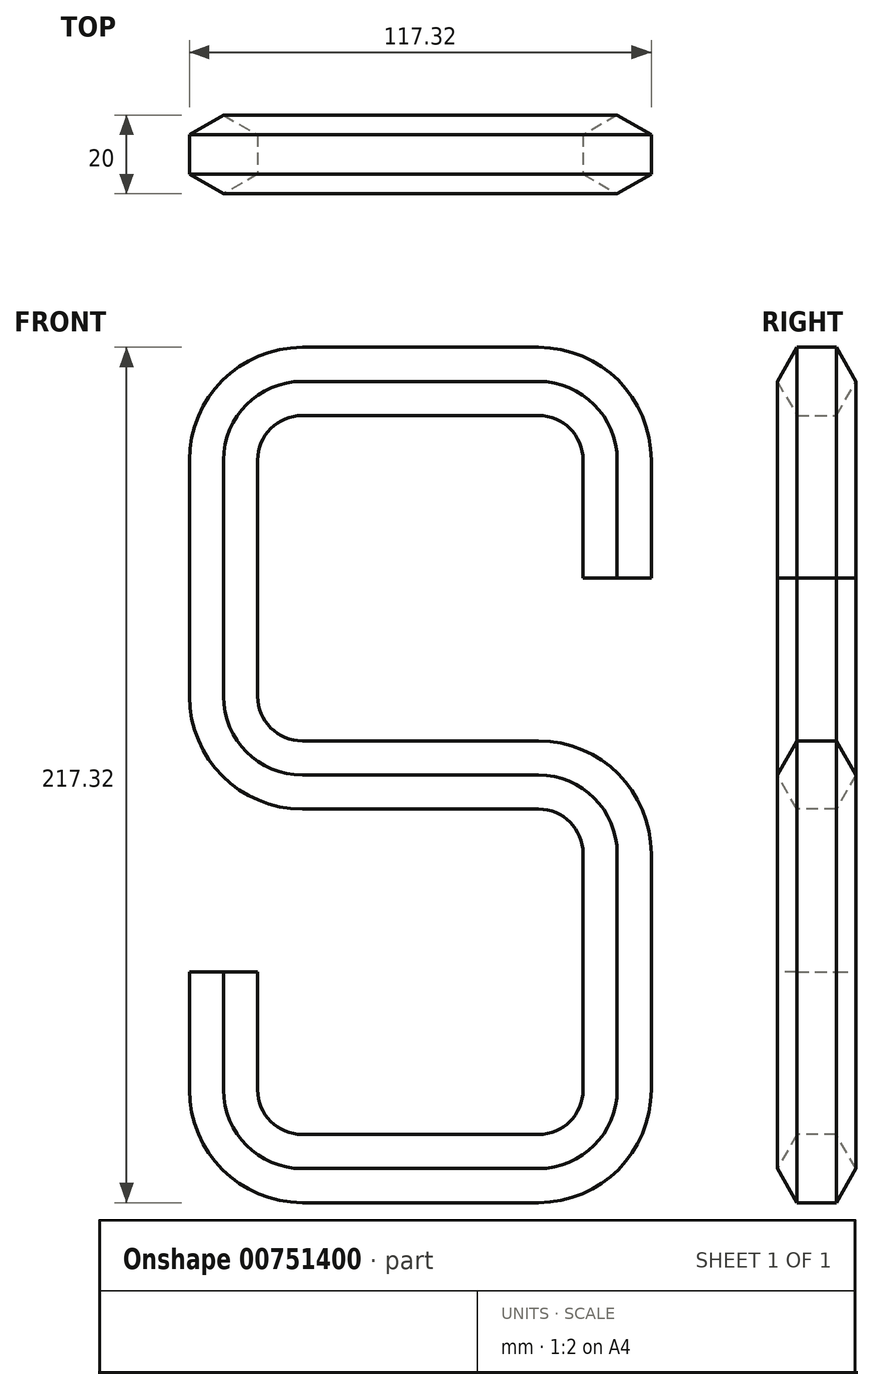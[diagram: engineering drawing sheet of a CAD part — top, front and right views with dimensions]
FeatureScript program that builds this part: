
annotation { "Feature Type Name" : "Feature", "Feature Type Description" : "" }
export const myFeature = defineFeature(function(context is Context, id is Id, definition is map)
    precondition{}
    {
        {
            var Q0;
            Q0=qCreatedBy(makeId("Front.planeOp"),FACE);
            var sketch = newSketch(context, id + "F0", { "sketchPlane" : qUnion([Q0])});
            skLineSegment(sketch, "E0", {"start": v(0, 0) * mm, "end": v(0, 30) * mm});
            skLineSegment(sketch, "E1", {"start": v(-20, 50) * mm, "end": v(-80, 50) * mm});
            skLineSegment(sketch, "E2", {"start": v(-100, 30) * mm, "end": v(-100, -30) * mm});
            skLineSegment(sketch, "E3", {"start": v(-80, -50) * mm, "end": v(-20, -50) * mm});
            skLineSegment(sketch, "E4", {"start": v(0, -70) * mm, "end": v(0, -130) * mm});
            skLineSegment(sketch, "E5", {"start": v(-20, -150) * mm, "end": v(-80, -150) * mm});
            skPoint(sketch, "E6.visualSharp", {"position": v(0, 50) * mm});
            skArc(sketch, "E6.filletArc", {"start": v(0, 30) * mm, "mid": v(-5.86, 44.14) * mm, "end": v(-20, 50) * mm});
            skPoint(sketch, "E7.visualSharp", {"position": v(-100, -50) * mm});
            skArc(sketch, "E7.filletArc", {"start": v(-100, -30) * mm, "mid": v(-94.14, -44.14) * mm, "end": v(-80, -50) * mm});
            skPoint(sketch, "E8.visualSharp", {"position": v(0, -50) * mm});
            skArc(sketch, "E8.filletArc", {"start": v(0, -70) * mm, "mid": v(-5.86, -55.86) * mm, "end": v(-20, -50) * mm});
            skPoint(sketch, "E9.visualSharp", {"position": v(0, -150) * mm});
            skArc(sketch, "E9.filletArc", {"start": v(-20, -150) * mm, "mid": v(-5.86, -144.14) * mm, "end": v(0, -130) * mm});
            skLineSegment(sketch, "E10", {"start": v(-100, -130) * mm, "end": v(-100, -100) * mm});
            skPoint(sketch, "E11.visualSharp", {"position": v(-100, -150) * mm});
            skArc(sketch, "E11.filletArc", {"start": v(-100, -130) * mm, "mid": v(-94.14, -144.14) * mm, "end": v(-80, -150) * mm});
            skPoint(sketch, "E12.visualSharp", {"position": v(-100, 50) * mm});
            skArc(sketch, "E12.filletArc", {"start": v(-80, 50) * mm, "mid": v(-94.14, 44.14) * mm, "end": v(-100, 30) * mm});
            skSolve(sketch);
        }
        {
            var Q0;
            Q0=qCreatedBy(makeId("Top.planeOp"),FACE);
            var sketch = newSketch(context, id + "F1", { "sketchPlane" : qUnion([Q0])});
            skCircle(sketch, "E13.cCircle", {"center": v(0, 0) * mm, "radius": 8.66 * mm, "construction": true});
            skLineSegment(sketch, "E13.0", {"start": v(8.66, 5) * mm, "end": v(8.66, -5) * mm});
            skLineSegment(sketch, "E13.1", {"start": v(8.66, -5) * mm, "end": v(0, -10) * mm});
            skLineSegment(sketch, "E13.2", {"start": v(0, -10) * mm, "end": v(-8.66, -5) * mm});
            skLineSegment(sketch, "E13.3", {"start": v(-8.66, -5) * mm, "end": v(-8.66, 5) * mm});
            skLineSegment(sketch, "E13.4", {"start": v(-8.66, 5) * mm, "end": v(0, 10) * mm});
            skLineSegment(sketch, "E13.5", {"start": v(0, 10) * mm, "end": v(8.66, 5) * mm});
            skPoint(sketch, "E13.0.midPoint", {"position": v(8.66, 0) * mm});
            skSolve(sketch);
        }
        {
            var Q0;
            Q0=makeQuery(id+"F1.imprint","IMPRINT",FACE,{"disambiguationData":[TD([[makeQuery(id+"F1.imprint","IMPRINT",EDGE,{"derivedFrom":sQuery(id+"F1.wireOp",EDGE,"E13.0")}),-1.0]])]});
            var Q1;
            Q1=sQuery(id+"F0.wireOp",EDGE,"E0");
            var Q2;
            Q2=sQuery(id+"F0.wireOp",EDGE,"E6.filletArc");
            var Q3;
            Q3=sQuery(id+"F0.wireOp",EDGE,"E1");
            var Q4;
            Q4=sQuery(id+"F0.wireOp",EDGE,"E12.filletArc");
            var Q5;
            Q5=sQuery(id+"F0.wireOp",EDGE,"E2");
            var Q6;
            Q6=sQuery(id+"F0.wireOp",EDGE,"E7.filletArc");
            var Q7;
            Q7=sQuery(id+"F0.wireOp",EDGE,"E3");
            var Q8;
            Q8=sQuery(id+"F0.wireOp",EDGE,"E8.filletArc");
            var Q9;
            Q9=sQuery(id+"F0.wireOp",EDGE,"E4");
            var Q10;
            Q10=sQuery(id+"F0.wireOp",EDGE,"E9.filletArc");
            var Q11;
            Q11=sQuery(id+"F0.wireOp",EDGE,"E5");
            var Q12;
            Q12=sQuery(id+"F0.wireOp",EDGE,"E11.filletArc");
            var Q13;
            Q13=sQuery(id+"F0.wireOp",EDGE,"E10");
            sweep(context, id + "F2", {"profiles" : qUnion([Q0]), "path" : qUnion([Q1, Q2, Q3, Q4, Q5, Q6, Q7, Q8, Q9, Q10, Q11, Q12, Q13])});
        }
    });
